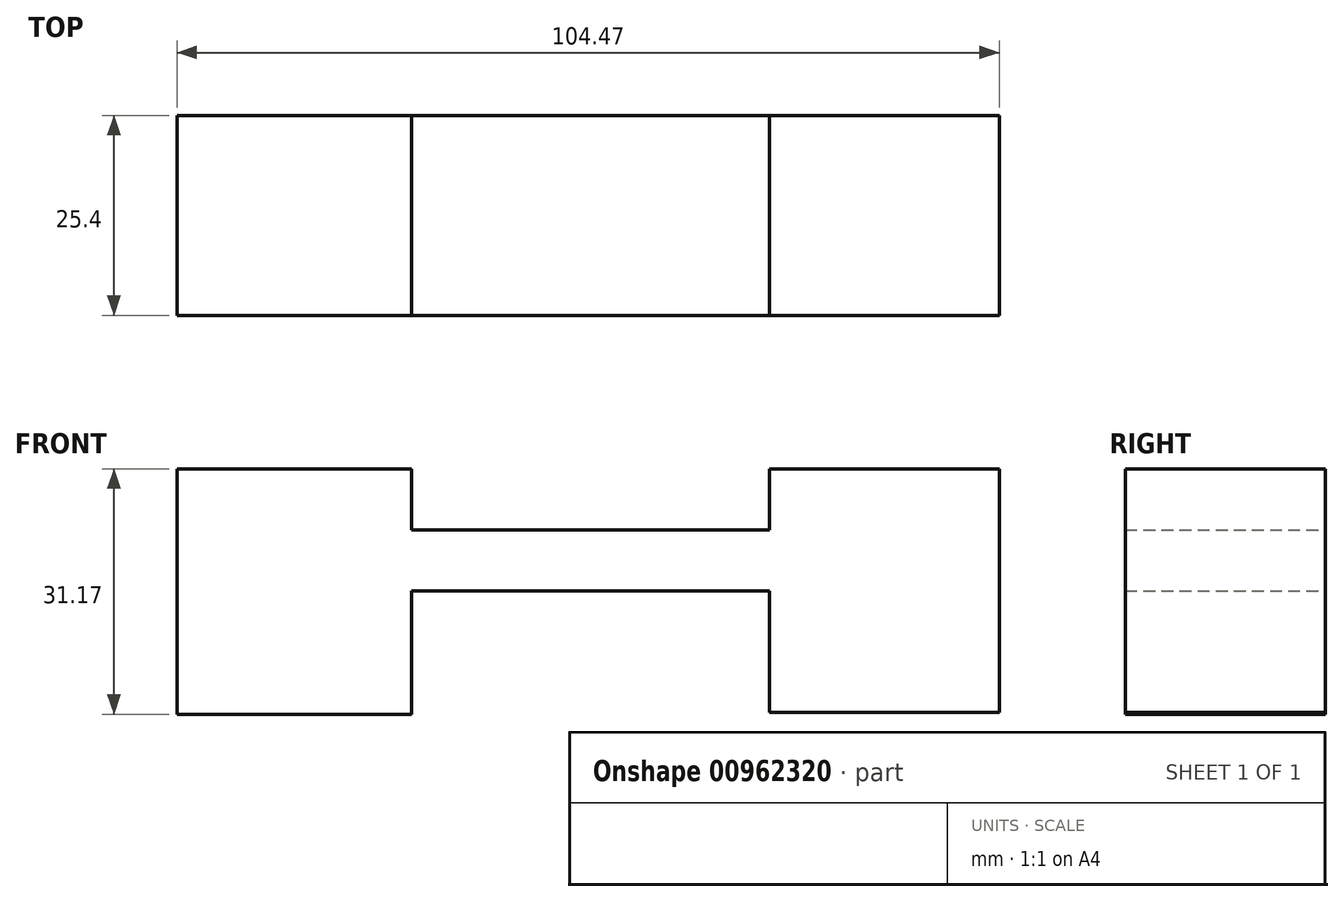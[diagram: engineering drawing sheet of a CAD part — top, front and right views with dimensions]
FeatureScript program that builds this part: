
annotation { "Feature Type Name" : "Feature", "Feature Type Description" : "" }
export const myFeature = defineFeature(function(context is Context, id is Id, definition is map)
    precondition{}
    {
        {
            var Q0;
            Q0=qCreatedBy(makeId("Front.planeOp"),FACE);
            var sketch = newSketch(context, id + "F0", { "sketchPlane" : qUnion([Q0])});
            skLineSegment(sketch, "E0.bottom", {"start": v(-51.98, 0) * mm, "end": v(-22.16, 0) * mm});
            skLineSegment(sketch, "E0.top", {"start": v(-51.98, -31.17) * mm, "end": v(-22.16, -31.17) * mm});
            skLineSegment(sketch, "E0.left", {"start": v(-51.98, 0) * mm, "end": v(-51.98, -31.17) * mm});
            skLineSegment(sketch, "E0.right", {"start": v(-22.16, 0) * mm, "end": v(-22.16, -31.17) * mm});
            skLineSegment(sketch, "E1.bottom", {"start": v(52.49, 0) * mm, "end": v(23.27, 0) * mm});
            skLineSegment(sketch, "E1.top", {"start": v(52.49, -30.97) * mm, "end": v(23.27, -30.97) * mm});
            skLineSegment(sketch, "E1.left", {"start": v(52.49, 0) * mm, "end": v(52.49, -30.97) * mm});
            skLineSegment(sketch, "E1.right", {"start": v(23.27, 0) * mm, "end": v(23.27, -30.97) * mm});
            skLineSegment(sketch, "E2.bottom", {"start": v(23.27, -15.49) * mm, "end": v(-22.16, -15.49) * mm});
            skLineSegment(sketch, "E2.top", {"start": v(23.27, -7.76) * mm, "end": v(-22.16, -7.76) * mm});
            skLineSegment(sketch, "E2.left", {"start": v(23.27, -15.49) * mm, "end": v(23.27, -7.76) * mm});
            skLineSegment(sketch, "E2.right", {"start": v(-22.16, -15.49) * mm, "end": v(-22.16, -7.76) * mm});
            skSolve(sketch);
        }
        {
            var Q0;
            Q0=qSketchRegion(id+"F0",true);
            extrude(context, id + "F1", {"entities" : qUnion([Q0]), "depth" : 25.4 * mm, "offsetDistance" : 25.4 * mm});
        }
    });
